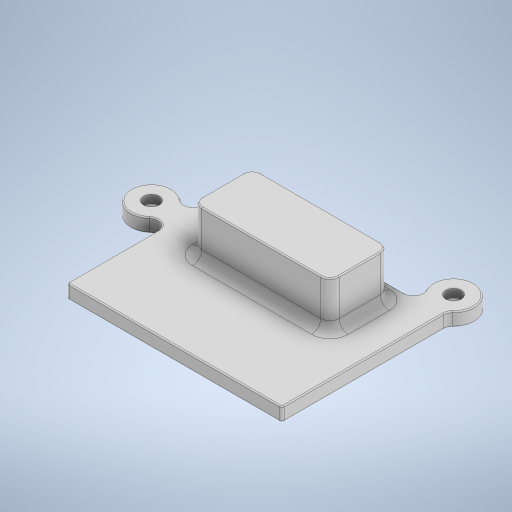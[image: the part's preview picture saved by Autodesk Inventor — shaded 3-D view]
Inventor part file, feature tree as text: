
AUTODESK INVENTOR PART (.ipt)
format: ipt  version: 2024.2 (Build 282272000, 272)  size: 403,456 bytes
history: native  units: mm
features: extrude x4, sketch x4, fillet x3
ambient origin geometry x8: Origin, YZ Plane, XZ Plane, XY Plane, X Axis, Y Axis, Z Axis, Center Point
bodies: Solid1 (feature_tree)
feature tree (11):
  extrude  "Extrusion1"  Depth=35.0mm
  extrude  "Extrusion3"  Depth=5.0mm
  extrude  "Extrusion4"  Depth=3.0mm TaperAngle=0.0deg
  fillet  "Fillet4"  Radius=2.5mm
  fillet  "Fillet5"  Radius=5.0mm
  fillet  "Fillet6"  Radius=50.8mm
  extrude  "Extrusion5"  Depth=0.2mm
  sketch  "Sketch1"  dims[d0=47.0mm d1=35.0mm]
  sketch  "Sketch3"  dims[d3=3.4mm d4=5.0mm]
  sketch  "Sketch4"  dims[d5=9.0mm d6=3.0mm d7=0.0mm d17=2.5mm d18=5.0mm d19=50.8mm]
  sketch  "Sketch5"  dims[d20=5.0mm d21=2.5mm d22=15.2mm d23=5.7mm d24=1.0mm d25=0.0mm d26=30.0mm d27=13.0mm d28=3.0mm d29=10.0mm d30=0.0mm d31=2.0mm d32=0.5mm d33=0.25mm d34=0.2mm d35=0.0mm]
